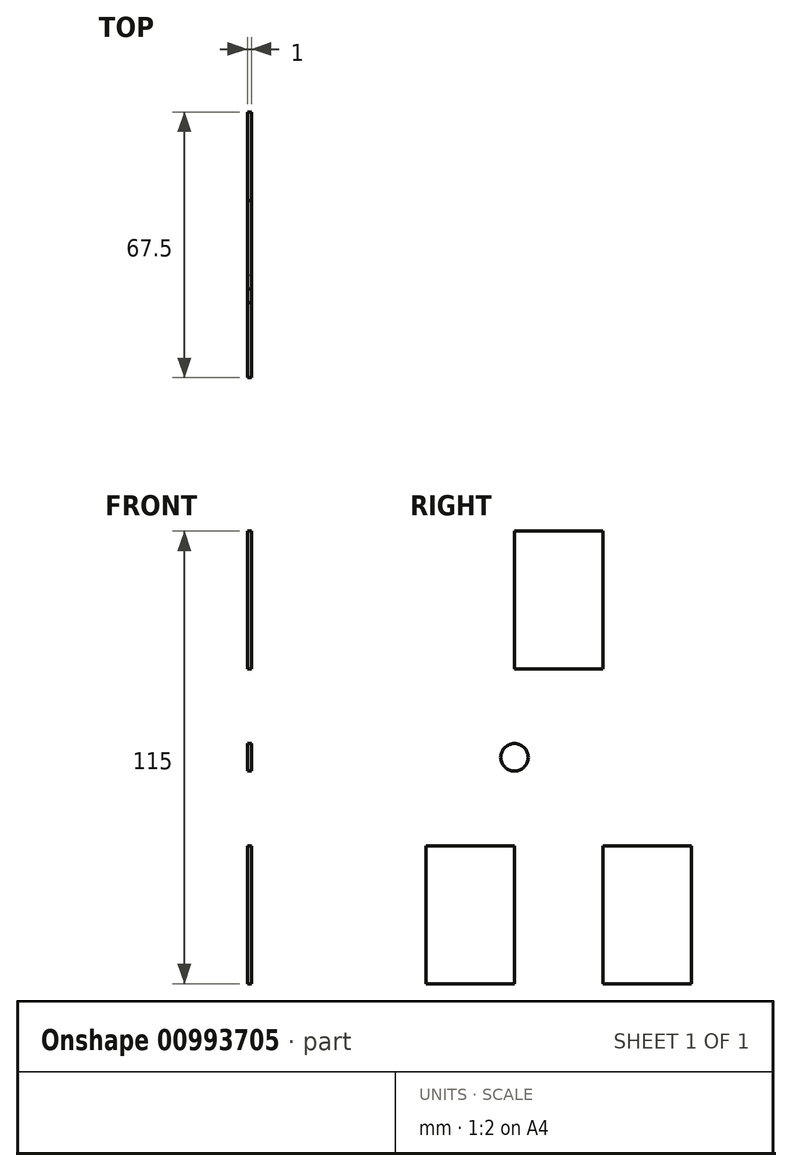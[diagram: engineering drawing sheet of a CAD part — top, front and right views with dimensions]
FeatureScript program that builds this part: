
annotation { "Feature Type Name" : "Feature", "Feature Type Description" : "" }
export const myFeature = defineFeature(function(context is Context, id is Id, definition is map)
    precondition{}
    {
        {
            var Q0;
            Q0=qCreatedBy(makeId("Right.planeOp"),FACE);
            var sketch = newSketch(context, id + "F0", { "sketchPlane" : qUnion([Q0])});
            skLineSegment(sketch, "E0.bottom", {"start": v(-45, 57.5) * mm, "end": v(45, 57.5) * mm});
            skLineSegment(sketch, "E0.top", {"start": v(-45, -57.5) * mm, "end": v(45, -57.5) * mm});
            skLineSegment(sketch, "E0.left", {"start": v(-45, 57.5) * mm, "end": v(-45, -57.5) * mm});
            skLineSegment(sketch, "E0.right", {"start": v(45, 57.5) * mm, "end": v(45, -57.5) * mm});
            skPoint(sketch, "E0.middle", {"position": v(0, 0) * mm});
            skLineSegment(sketch, "E1", {"start": v(-45, 57.5) * mm, "end": v(-45, 22.5) * mm});
            skLineSegment(sketch, "E2", {"start": v(-45, 22.5) * mm, "end": v(45, 22.5) * mm});
            skLineSegment(sketch, "E3", {"start": v(-45, -57.5) * mm, "end": v(-45, -22.5) * mm});
            skLineSegment(sketch, "E4", {"start": v(-45, -22.5) * mm, "end": v(-45, 0) * mm});
            skLineSegment(sketch, "E5", {"start": v(-45, 0) * mm, "end": v(-45, 22.5) * mm});
            skLineSegment(sketch, "E6", {"start": v(-45, -22.5) * mm, "end": v(45, -22.5) * mm});
            skLineSegment(sketch, "E7", {"start": v(45, -22.5) * mm, "end": v(45, 0) * mm});
            skLineSegment(sketch, "E8", {"start": v(45, 0) * mm, "end": v(45, 22.5) * mm});
            skLineSegment(sketch, "E9", {"start": v(0, -22.5) * mm, "end": v(0, -57.5) * mm});
            skLineSegment(sketch, "E10", {"start": v(0, -57.5) * mm, "end": v(-45, -57.5) * mm});
            skLineSegment(sketch, "E11", {"start": v(-22.5, -57.5) * mm, "end": v(-22.5, -22.5) * mm});
            skLineSegment(sketch, "E12", {"start": v(-22.5, -22.5) * mm, "end": v(0, -22.5) * mm});
            skLineSegment(sketch, "E13", {"start": v(0, -22.5) * mm, "end": v(45, -22.5) * mm});
            skLineSegment(sketch, "E14", {"start": v(22.5, -22.5) * mm, "end": v(22.5, -57.5) * mm});
            skLineSegment(sketch, "E15", {"start": v(0, 22.5) * mm, "end": v(45, 22.5) * mm});
            skLineSegment(sketch, "E16", {"start": v(0, 22.5) * mm, "end": v(-45, 22.5) * mm});
            skLineSegment(sketch, "E17", {"start": v(0, 22.5) * mm, "end": v(0, 57.5) * mm});
            skLineSegment(sketch, "E18", {"start": v(22.5, 22.5) * mm, "end": v(22.5, 57.5) * mm});
            skLineSegment(sketch, "E19", {"start": v(-22.5, 22.5) * mm, "end": v(-22.5, 57.5) * mm});
            skLineSegment(sketch, "E20", {"start": v(-45, 0) * mm, "end": v(-10, 0) * mm});
            skLineSegment(sketch, "E21", {"start": v(45, 0) * mm, "end": v(10, 0) * mm});
            skLineSegment(sketch, "E22", {"start": v(10, 0) * mm, "end": v(10, -22.5) * mm});
            skLineSegment(sketch, "E23", {"start": v(10, 0) * mm, "end": v(10, 22.5) * mm});
            skLineSegment(sketch, "E24", {"start": v(-10, 22.5) * mm, "end": v(-10, 0) * mm});
            skLineSegment(sketch, "E25", {"start": v(-10, 0) * mm, "end": v(-10, -22.5) * mm});
            skCircle(sketch, "E26", {"center": v(0, 0) * mm, "radius": 3.5 * mm});
            skSolve(sketch);
        }
        {
            var Q0;
            {var subQ0=sQuery(id+"F0.wireOp",EDGE,"E1");Q0=makeQuery(id+"F0.imprint","IMPRINT",FACE,{"disambiguationData":[TD([[makeQuery(id+"F0.imprint","IMPRINT",EDGE,{"derivedFrom":subQ0}),1.0]])]});}
            var Q1;
            Q1=makeQuery(id+"F0.imprint","IMPRINT",FACE,{"disambiguationData":[TD([[makeQuery(id+"F0.imprint","IMPRINT",EDGE,{"derivedFrom":sQuery(id+"F0.wireOp",EDGE,"E4")}),-1.0]])]});
            var Q2;
            {var subQ4=sQuery(id+"F0.wireOp",EDGE,"E9");Q2=makeQuery(id+"F0.imprint","IMPRINT",FACE,{"disambiguationData":[TD([[makeQuery(id+"F0.imprint","IMPRINT",EDGE,{"derivedFrom":subQ4}),-1.0]])]});}
            var Q3;
            {var subQ3=sQuery(id+"F0.wireOp",EDGE,"E14");Q3=makeQuery(id+"F0.imprint","IMPRINT",FACE,{"disambiguationData":[TD([[makeQuery(id+"F0.imprint","IMPRINT",EDGE,{"derivedFrom":subQ3}),1.0]])]});}
            var Q4;
            Q4=makeQuery(id+"F0.imprint","IMPRINT",FACE,{"disambiguationData":[TD([[makeQuery(id+"F0.imprint","IMPRINT",EDGE,{"derivedFrom":sQuery(id+"F0.wireOp",EDGE,"E26")}),1.0]])]});
            var Q5;
            {var subQ1=sQuery(id+"F0.wireOp",EDGE,"E8");Q5=makeQuery(id+"F0.imprint","IMPRINT",FACE,{"disambiguationData":[TD([[makeQuery(id+"F0.imprint","IMPRINT",EDGE,{"derivedFrom":subQ1}),1.0]])]});}
            var Q6;
            {var subQ0=sQuery(id+"F0.wireOp",EDGE,"E17");Q6=makeQuery(id+"F0.imprint","IMPRINT",FACE,{"disambiguationData":[TD([[makeQuery(id+"F0.imprint","IMPRINT",EDGE,{"derivedFrom":subQ0}),-1.0]])]});}
            extrude(context, id + "F1", {"entities" : qUnion([Q0, Q1, Q2, Q3, Q4, Q5, Q6]), "oppositeDirection" : true, "depth" : 1 * mm, "offsetDistance" : 25 * mm});
        }
    });
